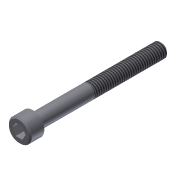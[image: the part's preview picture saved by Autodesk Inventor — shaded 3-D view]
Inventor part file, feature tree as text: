
AUTODESK INVENTOR PART (.ipt)
format: ipt  version: 2011 SP1 (Build 150282100, 282)  size: 99,328 bytes
history: native  units: in
note: dims shown in document units (in); Inventor stores cm internally (conversion verified against a paired STEP export)
features: extrude x3, sketch x3, chamfer x2, thread x1
ambient origin geometry x8: Origin, YZ Plane, XZ Plane, XY Plane, X Axis, Y Axis, Z Axis, Center Point
bodies: Solid1 (feature_tree)
feature tree (9):
  extrude  "Extrusion1"  Depth=0.19in TaperAngle=0.0deg
  extrude  "Extrusion2"  Depth=1.75in TaperAngle=0.0deg
  extrude  "Extrusion3"  Depth=0.125in TaperAngle=0.0deg
  thread  "Thread1"  [1 undecoded]
  chamfer  "Chamfer1"  Distance=0.02in Angle=45.0deg
  chamfer  "Chamfer2"  Distance=0.02in Angle=45.0deg
  sketch  "Sketch1"  dims[d0=0.312in d1=0.19in d2=0.0in]
  sketch  "Sketch2"  dims[d3=0.19in d4=1.75in d5=0.0in]
  sketch  "Sketch3"  dims[d6=0.1562in d7=0.125in d8=0.0in d9=1.0in d10=0.0in d11=0.02in d12=0.125in d13=45.0deg d14=0.02in d15=0.125in d16=45.0deg]
note: 1 required parameter value undecoded (feature->parameter linkage not recoverable at this tier; creation-order binding heuristic only, values carry confidence <= 0.55)
